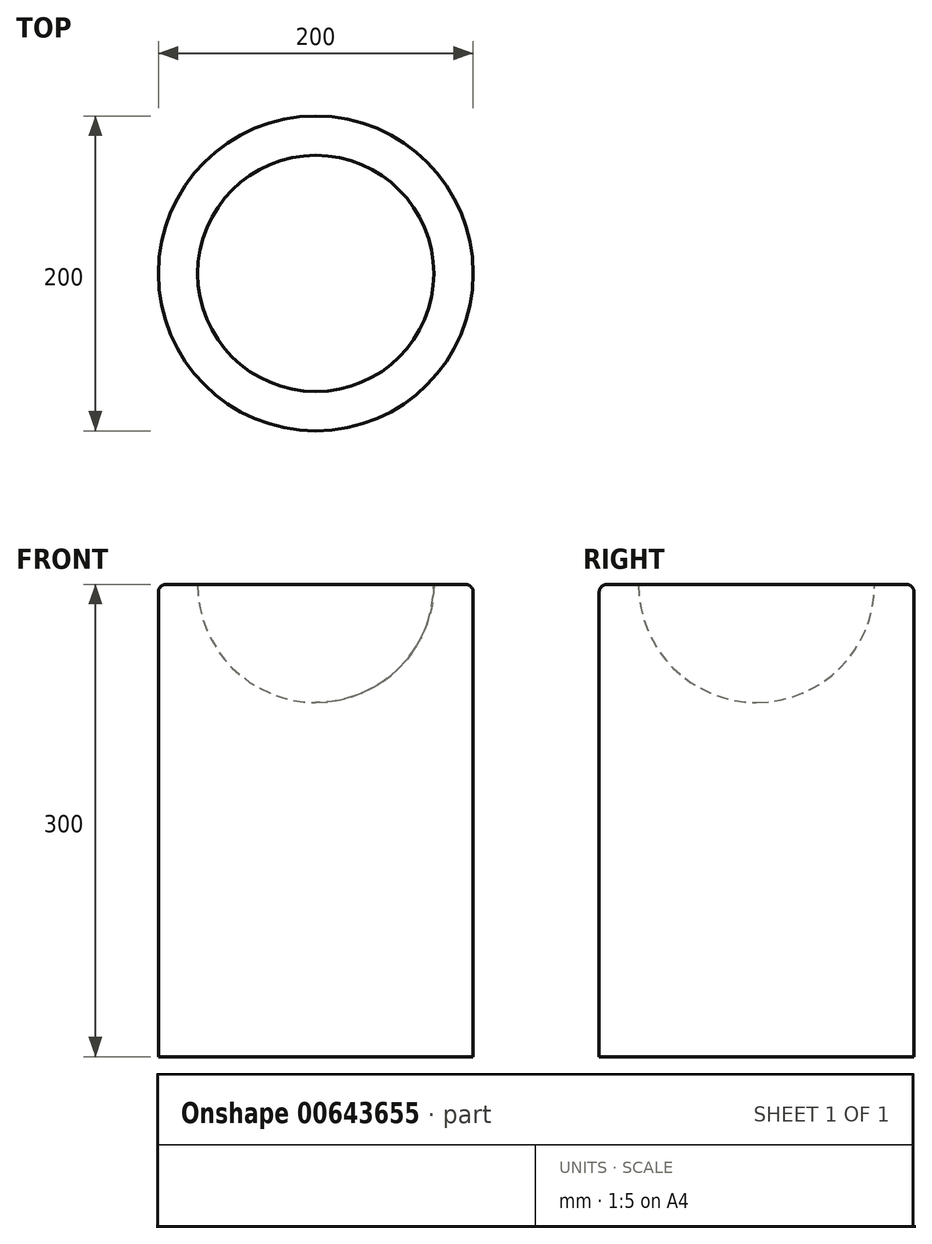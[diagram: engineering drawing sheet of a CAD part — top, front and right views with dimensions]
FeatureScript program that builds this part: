
annotation { "Feature Type Name" : "Feature", "Feature Type Description" : "" }
export const myFeature = defineFeature(function(context is Context, id is Id, definition is map)
    precondition{}
    {
        {
            var Q0;
            Q0=qCreatedBy(makeId("Top.planeOp"),FACE);
            var sketch = newSketch(context, id + "F0", { "sketchPlane" : qUnion([Q0])});
            skCircle(sketch, "E0", {"center": v(0, 0) * mm, "radius": 100 * mm});
            skSolve(sketch);
        }
        {
            var Q0;
            Q0=makeQuery(id+"F0.imprint","IMPRINT",FACE,{"disambiguationData":[TD([[makeQuery(id+"F0.imprint","IMPRINT",EDGE,{"derivedFrom":sQuery(id+"F0.wireOp",EDGE,"E0")}),1.0]])]});
            var Q1;
            Q1=sQuery(id+"F0.wireOp",EDGE,"E0");
            extrude(context, id + "F1", {"entities" : qUnion([Q0]), "surfaceEntities" : qUnion([Q1]), "oppositeDirection" : true, "depth" : 300 * mm, "offsetDistance" : 25 * mm});
        }
        {
            var Q0;
            Q0=qCreatedBy(makeId("Front.planeOp"),FACE);
            var sketch = newSketch(context, id + "F2", { "sketchPlane" : qUnion([Q0])});
            skArc(sketch, "E1", {"start": v(0, 75) * mm, "mid": v(-75, 0) * mm, "end": v(0, -75) * mm});
            skLineSegment(sketch, "E2", {"start": v(0, 75) * mm, "end": v(0, -75) * mm});
            skSolve(sketch);
        }
        {
            var Q0;
            Q0=makeQuery(id+"F2.imprint","IMPRINT",FACE,{"disambiguationData":[TD([[makeQuery(id+"F2.imprint","IMPRINT",EDGE,{"derivedFrom":sQuery(id+"F2.wireOp",EDGE,"E1")}),1.0]])]});
            var Q1;
            Q1=sQuery(id+"F2.wireOp",EDGE,"E2");
            revolve(context, id + "F3", {"operationType" : NewBodyOperationType.REMOVE, "entities" : qUnion([Q0]), "axis" : qUnion([Q1]), "revolveType" : RevolveType.FULL, "oppositeDirection" : true});
        }
        {
            var Q0;
            Q0=makeQuery(id+"F1.opExtrude","CAP_EDGE",EDGE,{"disambiguationData":[OSD([sQuery(id+"F0.wireOp",EDGE,"E0")])],"isStart":true});
            fillet(context, id + "F4", {"entities" : qUnion([Q0]), "radius" : 5 * mm, "tangentPropagation" : true, "allowEdgeOverflow" : false});
        }
    });
